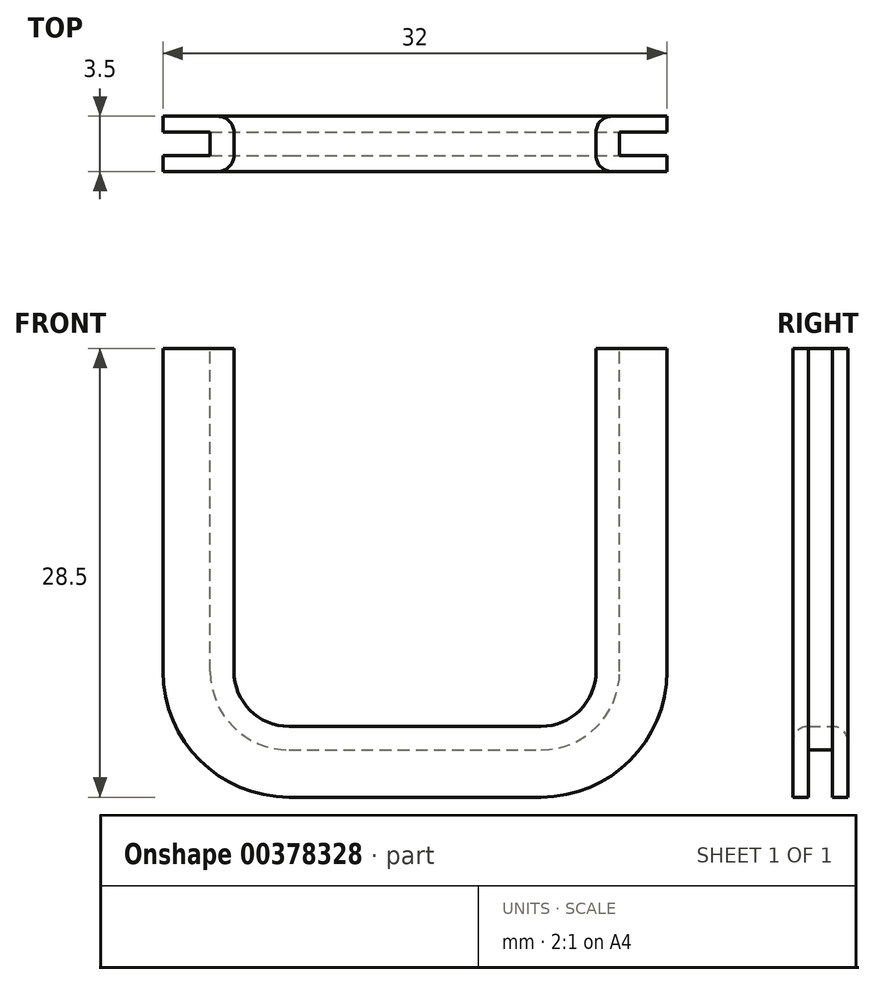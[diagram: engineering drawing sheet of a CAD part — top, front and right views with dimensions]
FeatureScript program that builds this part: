
annotation { "Feature Type Name" : "Feature", "Feature Type Description" : "" }
export const myFeature = defineFeature(function(context is Context, id is Id, definition is map)
    precondition{}
    {
        {
            var Q0;
            Q0=qCreatedBy(makeId("Front.planeOp"),FACE);
            var sketch = newSketch(context, id + "F0", { "sketchPlane" : qUnion([Q0])});
            skLineSegment(sketch, "E0.top", {"start": v(0, 25.5) * mm, "end": v(1.5, 25.5) * mm});
            skLineSegment(sketch, "E0.left", {"start": v(0, 5) * mm, "end": v(0, 25.5) * mm});
            skLineSegment(sketch, "E0.right", {"start": v(1.5, 5) * mm, "end": v(1.5, 25.5) * mm});
            skLineSegment(sketch, "E1.top", {"start": v(5, 1.5) * mm, "end": v(21, 1.5) * mm});
            skLineSegment(sketch, "E2.top", {"start": v(24.5, 25.5) * mm, "end": v(26, 25.5) * mm});
            skLineSegment(sketch, "E2.left", {"start": v(24.5, 5) * mm, "end": v(24.5, 25.5) * mm});
            skLineSegment(sketch, "E2.right", {"start": v(26, 5) * mm, "end": v(26, 25.5) * mm});
            skLineSegment(sketch, "E3", {"start": v(5, 0) * mm, "end": v(21, 0) * mm});
            skPoint(sketch, "E4.visualSharp", {"position": v(1.5, 1.5) * mm});
            skArc(sketch, "E4.filletArc", {"start": v(1.5, 5) * mm, "mid": v(2.53, 2.53) * mm, "end": v(5, 1.5) * mm});
            skPoint(sketch, "E5.visualSharp", {"position": v(24.5, 1.5) * mm});
            skArc(sketch, "E5.filletArc", {"start": v(21, 1.5) * mm, "mid": v(23.47, 2.53) * mm, "end": v(24.5, 5) * mm});
            skPoint(sketch, "E6.visualSharp", {"position": v(26, 0) * mm});
            skArc(sketch, "E6.filletArc", {"start": v(21, 0) * mm, "mid": v(24.54, 1.46) * mm, "end": v(26, 5) * mm});
            skPoint(sketch, "E7.visualSharp", {"position": v(0, 0) * mm});
            skArc(sketch, "E7.filletArc", {"start": v(0, 5) * mm, "mid": v(1.46, 1.46) * mm, "end": v(5, 0) * mm});
            skSolve(sketch);
        }
        {
            var Q0;
            Q0=qSketchRegion(id+"F0",true);
            extrude(context, id + "F1", {"entities" : qUnion([Q0]), "depth" : 1.5 * mm});
        }
        {
            var Q0;
            Q0=makeQuery(id+"F1.opExtrude","CAP_FACE",FACE,{"disambiguationData":[OSD([sQuery(id+"F0.wireOp",EDGE,"E0.top"),sQuery(id+"F0.wireOp",EDGE,"E0.left"),sQuery(id+"F0.wireOp",EDGE,"E0.right"),sQuery(id+"F0.wireOp",EDGE,"E1.top"),sQuery(id+"F0.wireOp",EDGE,"E2.top"),sQuery(id+"F0.wireOp",EDGE,"E2.left"),sQuery(id+"F0.wireOp",EDGE,"E2.right"),sQuery(id+"F0.wireOp",EDGE,"E3"),sQuery(id+"F0.wireOp",EDGE,"E4.filletArc"),sQuery(id+"F0.wireOp",EDGE,"E5.filletArc"),sQuery(id+"F0.wireOp",EDGE,"E6.filletArc"),sQuery(id+"F0.wireOp",EDGE,"E7.filletArc")])],"isStart":false});
            var sketch = newSketch(context, id + "F2", { "sketchPlane" : qUnion([Q0])});
            skLineSegment(sketch, "E8", {"start": v(1.5, 25.5) * mm, "end": v(-3, 25.5) * mm});
            skLineSegment(sketch, "E9", {"start": v(-3, 25.5) * mm, "end": v(-3, 5) * mm});
            skLineSegment(sketch, "E10", {"start": v(5, -3) * mm, "end": v(21, -3) * mm});
            skLineSegment(sketch, "E11", {"start": v(29, 5) * mm, "end": v(29, 25.5) * mm});
            skLineSegment(sketch, "E12", {"start": v(29, 25.5) * mm, "end": v(24.5, 25.5) * mm});
            skLineSegment(sketch, "E13", {"start": v(24.5, 25.5) * mm, "end": v(24.5, 5) * mm});
            skLineSegment(sketch, "E14", {"start": v(21, 1.5) * mm, "end": v(5, 1.5) * mm});
            skLineSegment(sketch, "E15", {"start": v(1.5, 5) * mm, "end": v(1.5, 25.5) * mm});
            skArc(sketch, "E16", {"start": v(1.5, 5) * mm, "mid": v(2.53, 2.53) * mm, "end": v(5, 1.5) * mm});
            skArc(sketch, "E17", {"start": v(21, 1.5) * mm, "mid": v(23.47, 2.53) * mm, "end": v(24.5, 5) * mm});
            skPoint(sketch, "E18.visualSharp", {"position": v(-3, -3) * mm});
            skArc(sketch, "E18.filletArc", {"start": v(-3, 5) * mm, "mid": v(-0.66, -0.66) * mm, "end": v(5, -3) * mm});
            skPoint(sketch, "E19.visualSharp", {"position": v(29, -3) * mm});
            skArc(sketch, "E19.filletArc", {"start": v(21, -3) * mm, "mid": v(26.66, -0.66) * mm, "end": v(29, 5) * mm});
            skSolve(sketch);
        }
        {
            var Q0;
            Q0=qSketchRegion(id+"F2",true);
            extrude(context, id + "F3", {"entities" : qUnion([Q0]), "operationType" : NewBodyOperationType.ADD, "depth" : 1 * mm});
        }
        {
            var Q0;
            Q0=makeQuery(id+"F1.opExtrude","CAP_FACE",FACE,{"disambiguationData":[OSD([sQuery(id+"F0.wireOp",EDGE,"E0.top"),sQuery(id+"F0.wireOp",EDGE,"E0.left"),sQuery(id+"F0.wireOp",EDGE,"E0.right"),sQuery(id+"F0.wireOp",EDGE,"E1.top"),sQuery(id+"F0.wireOp",EDGE,"E2.top"),sQuery(id+"F0.wireOp",EDGE,"E2.left"),sQuery(id+"F0.wireOp",EDGE,"E2.right"),sQuery(id+"F0.wireOp",EDGE,"E3"),sQuery(id+"F0.wireOp",EDGE,"E4.filletArc"),sQuery(id+"F0.wireOp",EDGE,"E5.filletArc"),sQuery(id+"F0.wireOp",EDGE,"E6.filletArc"),sQuery(id+"F0.wireOp",EDGE,"E7.filletArc")])],"isStart":true});
            var sketch = newSketch(context, id + "F4", { "sketchPlane" : qUnion([Q0])});
            skLineSegment(sketch, "E20", {"start": v(-24.5, 25.5) * mm, "end": v(-29, 25.5) * mm});
            skLineSegment(sketch, "E21", {"start": v(-29, 25.5) * mm, "end": v(-29, 5) * mm});
            skLineSegment(sketch, "E22", {"start": v(-21, -3) * mm, "end": v(-5, -3) * mm});
            skLineSegment(sketch, "E23", {"start": v(3, 5) * mm, "end": v(3, 25.5) * mm});
            skLineSegment(sketch, "E24", {"start": v(3, 25.5) * mm, "end": v(-1.5, 25.5) * mm});
            skLineSegment(sketch, "E25", {"start": v(-1.5, 25.5) * mm, "end": v(-1.5, 5) * mm});
            skLineSegment(sketch, "E26", {"start": v(-5, 1.5) * mm, "end": v(-21, 1.5) * mm});
            skLineSegment(sketch, "E27", {"start": v(-24.5, 5) * mm, "end": v(-24.5, 25.5) * mm});
            skArc(sketch, "E28", {"start": v(-24.5, 5) * mm, "mid": v(-23.47, 2.53) * mm, "end": v(-21, 1.5) * mm});
            skArc(sketch, "E29", {"start": v(-5, 1.5) * mm, "mid": v(-2.53, 2.53) * mm, "end": v(-1.5, 5) * mm});
            skArc(sketch, "E30", {"start": v(-29, 5) * mm, "mid": v(-26.66, -0.66) * mm, "end": v(-21, -3) * mm});
            skArc(sketch, "E31", {"start": v(-5, -3) * mm, "mid": v(0.66, -0.66) * mm, "end": v(3, 5) * mm});
            skSolve(sketch);
        }
        {
            var Q0;
            Q0=qSketchRegion(id+"F4",true);
            extrude(context, id + "F5", {"entities" : qUnion([Q0]), "operationType" : NewBodyOperationType.ADD, "depth" : 1 * mm});
        }
        {
            var Q0;
            Q0=makeQuery(id+"F5.opExtrude","CAP_EDGE",EDGE,{"disambiguationData":[OSD([sQuery(id+"F4.wireOp",EDGE,"E28")])],"isStart":false});
            var Q1;
            Q1=makeQuery(id+"F3.opExtrude","CAP_EDGE",EDGE,{"disambiguationData":[OSD([sQuery(id+"F2.wireOp",EDGE,"E13")])],"isStart":false});
            fillet(context, id + "F6", {"entities" : qUnion([Q0, Q1]), "radius" : 1 * mm, "tangentPropagation" : true, "allowEdgeOverflow" : false});
        }
    });
